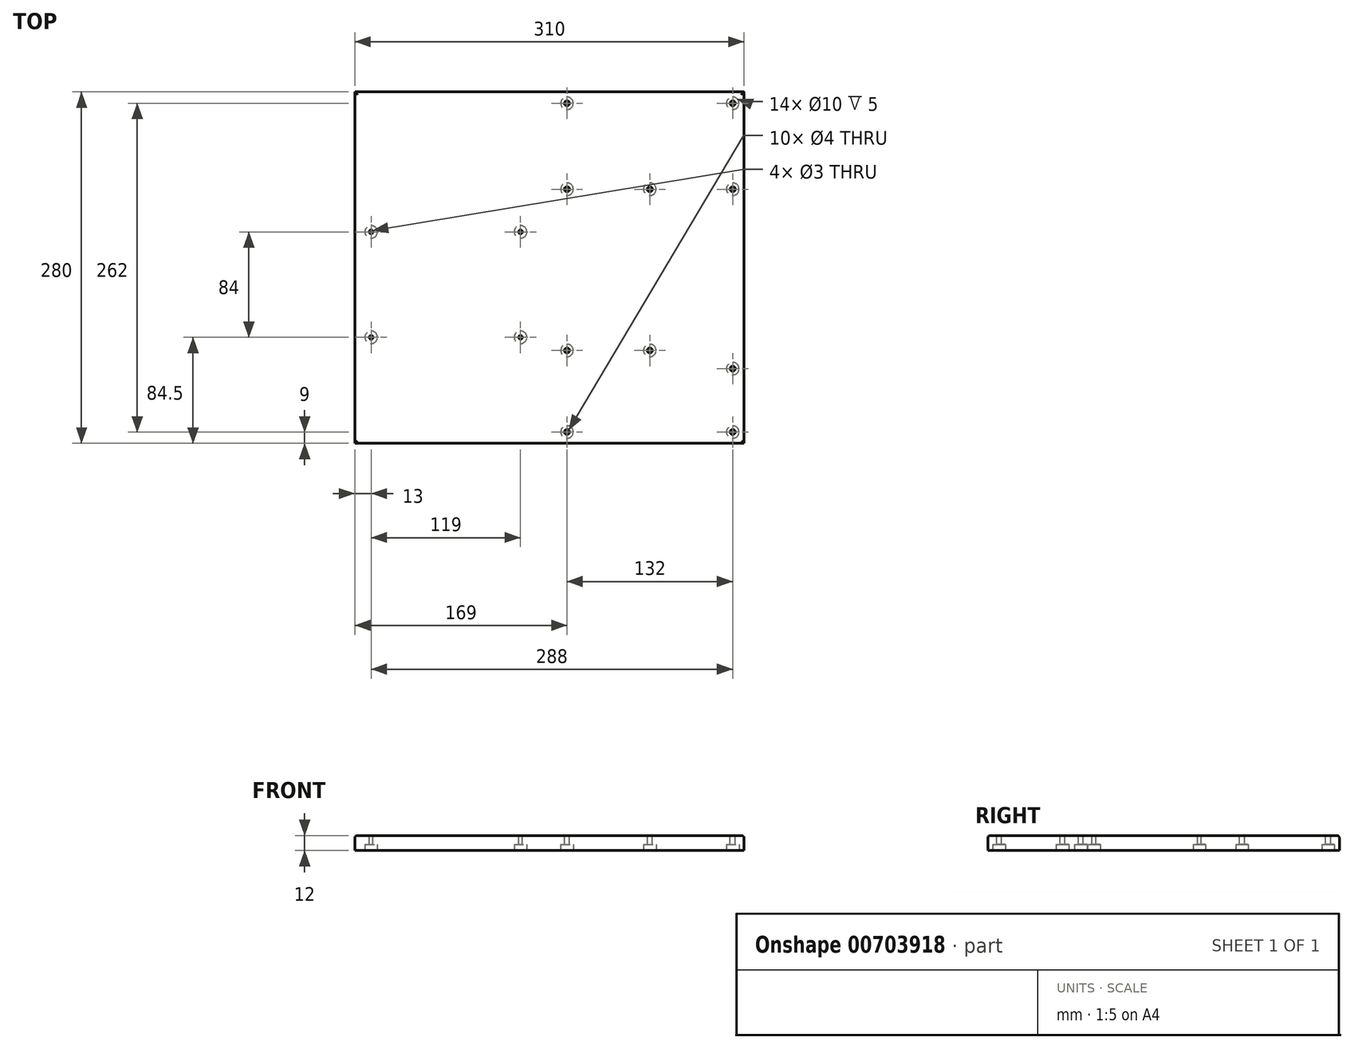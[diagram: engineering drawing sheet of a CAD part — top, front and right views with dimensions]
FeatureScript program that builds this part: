
annotation { "Feature Type Name" : "Feature", "Feature Type Description" : "" }
export const myFeature = defineFeature(function(context is Context, id is Id, definition is map)
    precondition{}
    {
        {
            var Q0;
            Q0=qCreatedBy(makeId("Top.planeOp"),FACE);
            var sketch = newSketch(context, id + "F0", { "sketchPlane" : qUnion([Q0])});
            skLineSegment(sketch, "E0.bottom", {"start": v(155, -140) * mm, "end": v(-155, -140) * mm});
            skLineSegment(sketch, "E0.top", {"start": v(155, 140) * mm, "end": v(-155, 140) * mm});
            skLineSegment(sketch, "E0.left", {"start": v(155, -140) * mm, "end": v(155, 140) * mm});
            skLineSegment(sketch, "E0.right", {"start": v(-155, -140) * mm, "end": v(-155, 140) * mm});
            skPoint(sketch, "E0.middle", {"position": v(0, 0) * mm});
            skSolve(sketch);
        }
        {
            var Q0;
            Q0=makeQuery(id+"F0.imprint","IMPRINT",FACE,{"disambiguationData":[TD([[makeQuery(id+"F0.imprint","IMPRINT",EDGE,{"derivedFrom":sQuery(id+"F0.wireOp",EDGE,"E0.bottom")}),-1.0]])]});
            extrude(context, id + "F1", {"entities" : qUnion([Q0]), "depth" : 12 * mm, "offsetDistance" : 25 * mm});
        }
        {
            var Q0;
            Q0=makeQuery(id+"F1.opExtrude","CAP_FACE",FACE,{"disambiguationData":[OSD([sQuery(id+"F0.wireOp",EDGE,"E0.bottom"),sQuery(id+"F0.wireOp",EDGE,"E0.top"),sQuery(id+"F0.wireOp",EDGE,"E0.left"),sQuery(id+"F0.wireOp",EDGE,"E0.right")])],"isStart":false});
            fillet(context, id + "F2", {"entities" : qUnion([Q0]), "radius" : 2 * mm, "tangentPropagation" : true, "allowEdgeOverflow" : false});
        }
        {
            var Q0;
            Q0=makeQuery(id+"F1.opExtrude","CAP_FACE",FACE,{"disambiguationData":[OSD([sQuery(id+"F0.wireOp",EDGE,"E0.bottom"),sQuery(id+"F0.wireOp",EDGE,"E0.top"),sQuery(id+"F0.wireOp",EDGE,"E0.left"),sQuery(id+"F0.wireOp",EDGE,"E0.right")])],"isStart":false});
            var sketch = newSketch(context, id + "F3", { "sketchPlane" : qUnion([Q0])});
            skLineSegment(sketch, "E1", {"start": v(-196.78, 0) * mm, "end": v(191.88, 0) * mm, "construction": true});
            skLineSegment(sketch, "E2", {"start": v(0, 157.57) * mm, "end": v(0, -128.27) * mm, "construction": true});
            skLineSegment(sketch, "E3", {"start": v(-200.75, 131) * mm, "end": v(221.24, 131) * mm, "construction": true});
            skLineSegment(sketch, "E4", {"start": v(-219.48, -131) * mm, "end": v(210.32, -131) * mm, "construction": true});
            skLineSegment(sketch, "E5", {"start": v(146, 162.68) * mm, "end": v(146, -159.38) * mm, "construction": true});
            skLineSegment(sketch, "E6", {"start": v(14, 134.7) * mm, "end": v(14, -161.99) * mm, "construction": true});
            skCircle(sketch, "E7", {"center": v(14, -131) * mm, "radius": 2 * mm});
            skCircle(sketch, "E8", {"center": v(14, 131) * mm, "radius": 2 * mm});
            skCircle(sketch, "E9", {"center": v(146, 131) * mm, "radius": 2 * mm});
            skCircle(sketch, "E10", {"center": v(146, -131) * mm, "radius": 2 * mm});
            skCircle(sketch, "E11", {"center": v(146, 62.5) * mm, "radius": 2 * mm});
            skCircle(sketch, "E12", {"center": v(146, -80.5) * mm, "radius": 2 * mm});
            skCircle(sketch, "E13", {"center": v(14, -66) * mm, "radius": 2 * mm});
            skCircle(sketch, "E14", {"center": v(14, 62.5) * mm, "radius": 2 * mm});
            skLineSegment(sketch, "E15", {"start": v(80, 143.04) * mm, "end": v(80, -143.04) * mm, "construction": true});
            skCircle(sketch, "E16", {"center": v(80, 62.5) * mm, "radius": 2 * mm});
            skCircle(sketch, "E17", {"center": v(80, -66) * mm, "radius": 2 * mm});
            skSolve(sketch);
        }
        {
            var Q0;
            Q0 = qSketchRegion(id + "F3", true);
            extrude(context, id + "F4", {"entities" : qUnion([Q0]), "operationType" : NewBodyOperationType.REMOVE, "oppositeDirection" : true, "depth" : 25 * mm, "offsetDistance" : 25 * mm});
        }
        {
            var Q0;
            Q0=makeQuery(id+"F1.opExtrude","CAP_FACE",FACE,{"disambiguationData":[OSD([sQuery(id+"F0.wireOp",EDGE,"E0.bottom"),sQuery(id+"F0.wireOp",EDGE,"E0.top"),sQuery(id+"F0.wireOp",EDGE,"E0.left"),sQuery(id+"F0.wireOp",EDGE,"E0.right")])],"isStart":true});
            var sketch = newSketch(context, id + "F5", { "sketchPlane" : qUnion([Q0])});
            skCircle(sketch, "E18", {"center": v(14, 131) * mm, "radius": 5 * mm});
            skCircle(sketch, "E19", {"center": v(14, 66) * mm, "radius": 5 * mm});
            skCircle(sketch, "E20", {"center": v(146, 80.5) * mm, "radius": 5 * mm});
            skCircle(sketch, "E21", {"center": v(146, 131) * mm, "radius": 5 * mm});
            skCircle(sketch, "E22", {"center": v(146, -62.5) * mm, "radius": 5 * mm});
            skCircle(sketch, "E23", {"center": v(14, -62.5) * mm, "radius": 5 * mm});
            skCircle(sketch, "E24", {"center": v(14, -131) * mm, "radius": 5 * mm});
            skCircle(sketch, "E25", {"center": v(146, -131) * mm, "radius": 5 * mm});
            skCircle(sketch, "E26", {"center": v(80, -62.5) * mm, "radius": 5 * mm});
            skCircle(sketch, "E27", {"center": v(80, 66) * mm, "radius": 5 * mm});
            skSolve(sketch);
        }
        {
            var Q0;
            Q0 = qSketchRegion(id + "F5", true);
            extrude(context, id + "F6", {"entities" : qUnion([Q0]), "operationType" : NewBodyOperationType.REMOVE, "oppositeDirection" : true, "depth" : 5 * mm, "offsetDistance" : 25 * mm});
        }
        {
            var Q0;
            Q0=makeQuery(id+"F1.opExtrude","CAP_FACE",FACE,{"disambiguationData":[OSD([sQuery(id+"F0.wireOp",EDGE,"E0.bottom"),sQuery(id+"F0.wireOp",EDGE,"E0.top"),sQuery(id+"F0.wireOp",EDGE,"E0.left"),sQuery(id+"F0.wireOp",EDGE,"E0.right")])],"isStart":false});
            var sketch = newSketch(context, id + "F7", { "sketchPlane" : qUnion([Q0])});
            skLineSegment(sketch, "E28", {"start": v(130.13, -55.5) * mm, "end": v(-146.46, -55.5) * mm, "construction": true});
            skPoint(sketch, "E29", {"position": v(14, -66) * mm});
            skLineSegment(sketch, "E30", {"start": v(111.7, 28.5) * mm, "end": v(-150.71, 28.5) * mm, "construction": true});
            skLineSegment(sketch, "E31", {"start": v(-23, 50.44) * mm, "end": v(-23, -80.35) * mm, "construction": true});
            skLineSegment(sketch, "E32", {"start": v(-142, 63.64) * mm, "end": v(-142, -75.13) * mm, "construction": true});
            skCircle(sketch, "E33", {"center": v(-142, 28.5) * mm, "radius": 1.5 * mm});
            skCircle(sketch, "E34", {"center": v(-23, 28.5) * mm, "radius": 1.5 * mm});
            skCircle(sketch, "E35", {"center": v(-23, -55.5) * mm, "radius": 1.5 * mm});
            skCircle(sketch, "E36", {"center": v(-142, -55.5) * mm, "radius": 1.5 * mm});
            skSolve(sketch);
        }
        {
            var Q0;
            Q0 = qSketchRegion(id + "F7", true);
            extrude(context, id + "F8", {"entities" : qUnion([Q0]), "operationType" : NewBodyOperationType.REMOVE, "oppositeDirection" : true, "depth" : 25 * mm, "offsetDistance" : 25 * mm});
        }
        {
            var Q0;
            Q0=makeQuery(id+"F1.opExtrude","CAP_FACE",FACE,{"disambiguationData":[OSD([sQuery(id+"F0.wireOp",EDGE,"E0.bottom"),sQuery(id+"F0.wireOp",EDGE,"E0.top"),sQuery(id+"F0.wireOp",EDGE,"E0.left"),sQuery(id+"F0.wireOp",EDGE,"E0.right")])],"isStart":true});
            var sketch = newSketch(context, id + "F9", { "sketchPlane" : qUnion([Q0])});
            skCircle(sketch, "E37", {"center": v(-142, 55.5) * mm, "radius": 5 * mm});
            skCircle(sketch, "E38", {"center": v(-142, -28.5) * mm, "radius": 5 * mm});
            skCircle(sketch, "E39", {"center": v(-23, -28.5) * mm, "radius": 5 * mm});
            skCircle(sketch, "E40", {"center": v(-23, 55.5) * mm, "radius": 5 * mm});
            skSolve(sketch);
        }
        {
            var Q0;
            Q0 = qSketchRegion(id + "F9", true);
            extrude(context, id + "F10", {"entities" : qUnion([Q0]), "operationType" : NewBodyOperationType.REMOVE, "oppositeDirection" : true, "depth" : 5 * mm, "offsetDistance" : 25 * mm});
        }
    });
